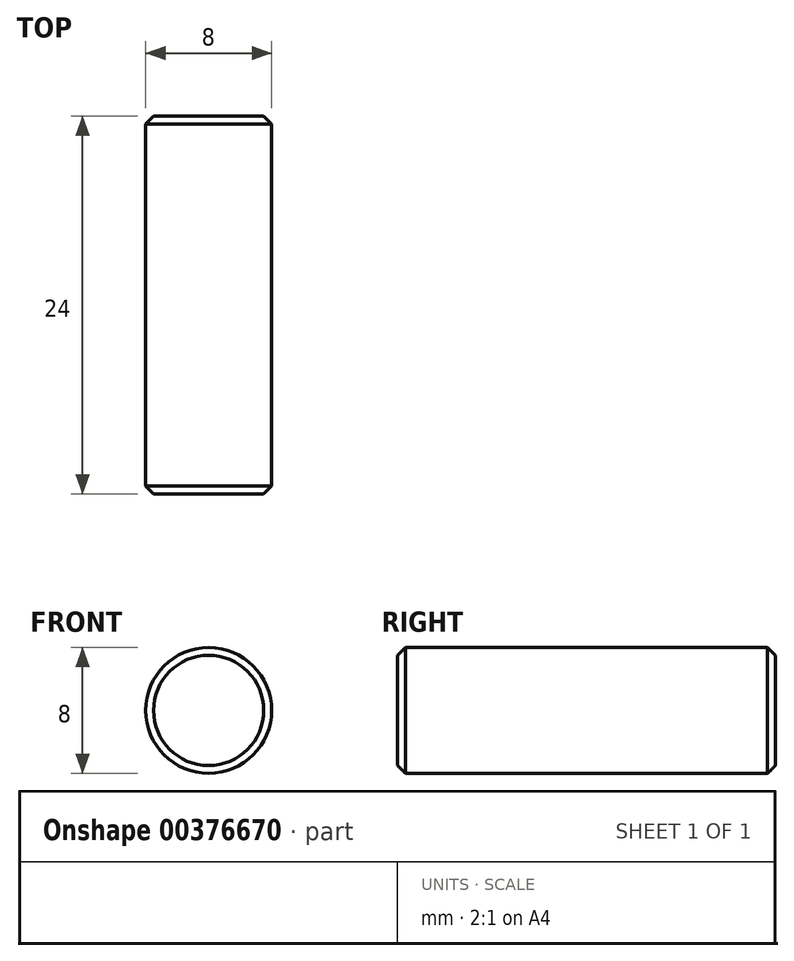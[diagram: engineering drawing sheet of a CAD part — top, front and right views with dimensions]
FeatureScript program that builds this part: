
annotation { "Feature Type Name" : "Feature", "Feature Type Description" : "" }
export const myFeature = defineFeature(function(context is Context, id is Id, definition is map)
    precondition{}
    {
        {
            var Q0;
            Q0=qCreatedBy(makeId("Right.planeOp"),FACE);
            var sketch = newSketch(context, id + "F0", { "sketchPlane" : qUnion([Q0])});
            skLineSegment(sketch, "E0.bottom", {"start": v(-12, 0) * mm, "end": v(12, 0) * mm});
            skLineSegment(sketch, "E0.top", {"start": v(-12, 7.5) * mm, "end": v(12, 7.5) * mm});
            skLineSegment(sketch, "E0.left", {"start": v(-12, 0) * mm, "end": v(-12, 7.5) * mm});
            skLineSegment(sketch, "E0.right", {"start": v(12, 0) * mm, "end": v(12, 7.5) * mm});
            skPoint(sketch, "E1", {"position": v(0, 0) * mm});
            skLineSegment(sketch, "E2.bottom", {"start": v(-8.75, 7.5) * mm, "end": v(-7.65, 7.5) * mm});
            skLineSegment(sketch, "E2.top", {"start": v(-8.75, 7.15) * mm, "end": v(-7.65, 7.15) * mm});
            skLineSegment(sketch, "E2.left", {"start": v(-8.75, 7.5) * mm, "end": v(-8.75, 7.15) * mm});
            skLineSegment(sketch, "E2.right", {"start": v(-7.65, 7.5) * mm, "end": v(-7.65, 7.15) * mm});
            skLineSegment(sketch, "E3", {"start": v(0, 0) * mm, "end": v(0, 12.3) * mm, "construction": true});
            skLineSegment(sketch, "E4.MirrorCS", {"start": v(7.65, 7.5) * mm, "end": v(7.65, 7.15) * mm});
            skLineSegment(sketch, "E5.MirrorCS", {"start": v(8.75, 7.5) * mm, "end": v(7.65, 7.5) * mm});
            skLineSegment(sketch, "E6.MirrorCS", {"start": v(8.75, 7.5) * mm, "end": v(8.75, 7.15) * mm});
            skLineSegment(sketch, "E7.MirrorCS", {"start": v(8.75, 7.15) * mm, "end": v(7.65, 7.15) * mm});
            skLineSegment(sketch, "E8.top", {"start": v(-12, 4) * mm, "end": v(12, 4) * mm});
            skLineSegment(sketch, "E8.left", {"start": v(-12, 0) * mm, "end": v(-12, 4) * mm});
            skLineSegment(sketch, "E8.right", {"start": v(12, 0) * mm, "end": v(12, 4) * mm});
            skLineSegment(sketch, "E9.MirrorCS", {"start": v(8.75, -7.15) * mm, "end": v(7.65, -7.15) * mm});
            skLineSegment(sketch, "E10.MirrorCS", {"start": v(8.75, -7.5) * mm, "end": v(7.65, -7.5) * mm});
            skLineSegment(sketch, "E11.MirrorCS", {"start": v(-8.75, -7.5) * mm, "end": v(-8.75, -7.15) * mm});
            skLineSegment(sketch, "E12.MirrorCS", {"start": v(7.65, -7.5) * mm, "end": v(7.65, -7.15) * mm});
            skLineSegment(sketch, "E13.MirrorCS", {"start": v(-7.65, -7.5) * mm, "end": v(-7.65, -7.15) * mm});
            skLineSegment(sketch, "E14.MirrorCS", {"start": v(8.75, -7.5) * mm, "end": v(8.75, -7.15) * mm});
            skLineSegment(sketch, "E15.MirrorCS", {"start": v(-12, 0) * mm, "end": v(-12, -7.5) * mm});
            skLineSegment(sketch, "E16.MirrorCS", {"start": v(-12, -7.5) * mm, "end": v(12, -7.5) * mm});
            skLineSegment(sketch, "E17.MirrorCS", {"start": v(12, 0) * mm, "end": v(12, -7.5) * mm});
            skLineSegment(sketch, "E18.MirrorCS", {"start": v(-8.75, -7.15) * mm, "end": v(-7.65, -7.15) * mm});
            skLineSegment(sketch, "E19.MirrorCS", {"start": v(-12, -4) * mm, "end": v(12, -4) * mm});
            skLineSegment(sketch, "E20.MirrorCS", {"start": v(12, 0) * mm, "end": v(12, -4) * mm});
            skLineSegment(sketch, "E21.MirrorCS", {"start": v(-8.75, -7.5) * mm, "end": v(-7.65, -7.5) * mm});
            skLineSegment(sketch, "E22.MirrorCS", {"start": v(-12, 0) * mm, "end": v(-12, -4) * mm});
            skSolve(sketch);
        }
        {
            var Q0;
            {var subQ5=sQuery(id+"F0.wireOp",EDGE,"E0.left");Q0=makeQuery(id+"F0.imprint","IMPRINT",FACE,{"disambiguationData":[TD([[makeQuery(id+"F0.imprint","IMPRINT",EDGE,{"derivedFrom":subQ5}),-1.0]])]});}
            var Q1;
            Q1=sQuery(id+"F0.wireOp",EDGE,"E0.bottom");
            revolve(context, id + "F1", {"surfaceOperationType" : NewSurfaceOperationType.NEW, "entities" : qUnion([Q0]), "axis" : qUnion([Q1]), "revolveType" : RevolveType.FULL});
        }
        {
            var Q0;
            Q0=makeQuery(id+"F1.opRevolve","SWEPT_EDGE",EDGE,{"disambiguationData":[OSD([sQuery(id+"F0.wireOp",EDGE,"E0.top"),sQuery(id+"F0.wireOp",EDGE,"E0.left")])]});
            var Q1;
            Q1=makeQuery(id+"F1.opRevolve","SWEPT_EDGE",EDGE,{"disambiguationData":[OSD([sQuery(id+"F0.wireOp",EDGE,"E0.top"),sQuery(id+"F0.wireOp",EDGE,"E0.right")])]});
            chamfer(context, id + "F2", {"entities" : qUnion([Q0, Q1]), "width" : .5 * mm, "tangentPropagation" : true});
        }
    });
